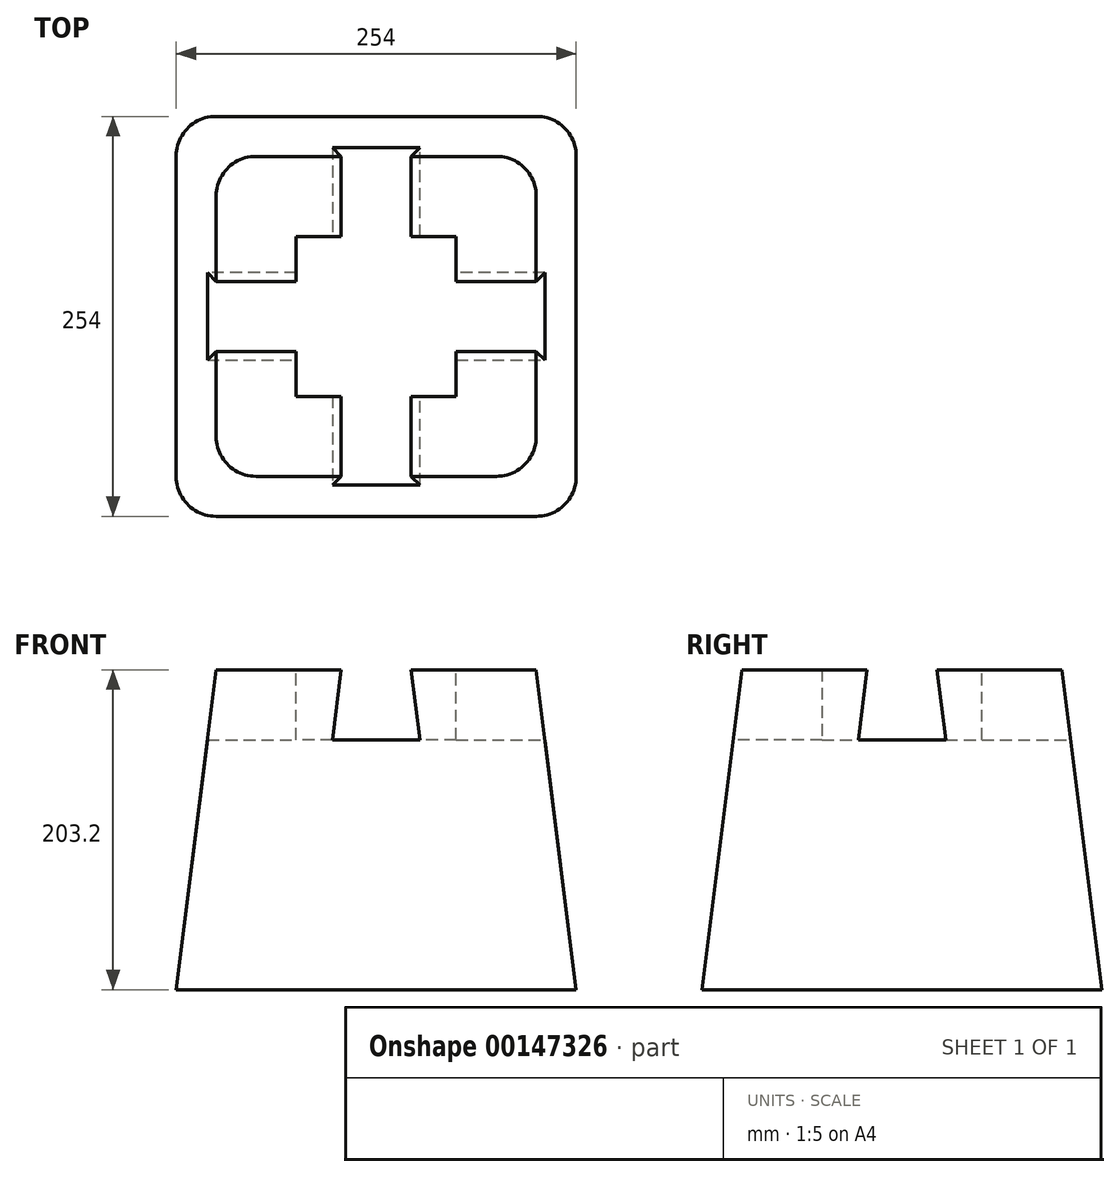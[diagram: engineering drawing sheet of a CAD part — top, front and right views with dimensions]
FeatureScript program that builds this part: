
annotation { "Feature Type Name" : "Feature", "Feature Type Description" : "" }
export const myFeature = defineFeature(function(context is Context, id is Id, definition is map)
    precondition{}
    {
        {
            var Q0;
            Q0=qCreatedBy(makeId("Top.planeOp"),FACE);
            var sketch = newSketch(context, id + "F0", { "sketchPlane" : qUnion([Q0])});
            skLineSegment(sketch, "E0.bottom", {"start": v(-127.47, 138) * mm, "end": v(126.53, 138) * mm});
            skLineSegment(sketch, "E0.top", {"start": v(-127.47, -116) * mm, "end": v(126.53, -116) * mm});
            skLineSegment(sketch, "E0.left", {"start": v(-127.47, 138) * mm, "end": v(-127.47, -116) * mm});
            skLineSegment(sketch, "E0.right", {"start": v(126.53, 138) * mm, "end": v(126.53, -116) * mm});
            skSolve(sketch);
        }
        {
            var Q0;
            Q0=qSketchRegion(id+"F0",true);
            extrude(context, id + "F1", {"entities" : qUnion([Q0]), "depth" : 203.2 * mm, "hasDraft" : true, "draftAngle" : 7.12 * degree, "draftPullDirection" : true});
        }
        {
            var Q0;
            Q0=makeQuery(id+"F1.opExtrude","SWEPT_EDGE",EDGE,{"disambiguationData":[OSD([sQuery(id+"F0.wireOp",EDGE,"E0.top"),sQuery(id+"F0.wireOp",EDGE,"E0.left")])]});
            var Q1;
            Q1=makeQuery(id+"F1.opExtrude","SWEPT_EDGE",EDGE,{"disambiguationData":[OSD([sQuery(id+"F0.wireOp",EDGE,"E0.top"),sQuery(id+"F0.wireOp",EDGE,"E0.right")])]});
            var Q2;
            Q2=makeQuery(id+"F1.opExtrude","SWEPT_EDGE",EDGE,{"disambiguationData":[OSD([sQuery(id+"F0.wireOp",EDGE,"E0.bottom"),sQuery(id+"F0.wireOp",EDGE,"E0.right")])]});
            var Q3;
            Q3=makeQuery(id+"F1.opExtrude","SWEPT_EDGE",EDGE,{"disambiguationData":[OSD([sQuery(id+"F0.wireOp",EDGE,"E0.bottom"),sQuery(id+"F0.wireOp",EDGE,"E0.left")])]});
            fillet(context, id + "F2", {"entities" : qUnion([Q0, Q1, Q2, Q3]), "radius" : 25.4 * mm, "tangentPropagation" : true, "allowEdgeOverflow" : false});
        }
        {
            var Q0;
            Q0=makeQuery(id+"F1.opExtrude","CAP_FACE",FACE,{"disambiguationData":[OSD([sQuery(id+"F0.wireOp",EDGE,"E0.bottom"),sQuery(id+"F0.wireOp",EDGE,"E0.top"),sQuery(id+"F0.wireOp",EDGE,"E0.left"),sQuery(id+"F0.wireOp",EDGE,"E0.right")])],"isStart":false});
            var sketch = newSketch(context, id + "F3", { "sketchPlane" : qUnion([Q0])});
            skLineSegment(sketch, "E1.0", {"start": v(-102.07, 33.23) * mm, "end": v(-102.07, -11.22) * mm});
            skLineSegment(sketch, "E2.0", {"start": v(-22.7, 112.6) * mm, "end": v(21.76, 112.6) * mm});
            skLineSegment(sketch, "E3.0", {"start": v(-22.7, -90.6) * mm, "end": v(21.76, -90.6) * mm});
            skLineSegment(sketch, "E4.0", {"start": v(101.13, 33.23) * mm, "end": v(101.13, -11.22) * mm});
            skLineSegment(sketch, "E5.bottom", {"start": v(-102.07, -11.22) * mm, "end": v(-22.7, -11.22) * mm});
            skLineSegment(sketch, "E5.top", {"start": v(-102.07, 33.23) * mm, "end": v(-22.7, 33.23) * mm});
            skLineSegment(sketch, "E5.left", {"start": v(-102.07, -11.22) * mm, "end": v(-102.07, 33.23) * mm});
            skLineSegment(sketch, "E5.right", {"start": v(101.13, -11.22) * mm, "end": v(101.13, 33.23) * mm});
            skLineSegment(sketch, "E6.left", {"start": v(-22.7, -90.6) * mm, "end": v(-22.7, -11.22) * mm});
            skLineSegment(sketch, "E6.right", {"start": v(21.76, -90.6) * mm, "end": v(21.76, -11.22) * mm});
            skLineSegment(sketch, "E7.trimOffspring", {"start": v(-22.7, 33.23) * mm, "end": v(-22.7, 112.6) * mm});
            skLineSegment(sketch, "E8.trimOffspring", {"start": v(21.76, 33.23) * mm, "end": v(101.13, 33.23) * mm});
            skLineSegment(sketch, "E9.trimOffspring", {"start": v(21.76, 33.23) * mm, "end": v(21.76, 112.6) * mm});
            skLineSegment(sketch, "E10.trimOffspring", {"start": v(21.76, -11.22) * mm, "end": v(101.13, -11.22) * mm});
            skPoint(sketch, "E11.orphan", {"position": v(101.13, -65.4) * mm});
            skPoint(sketch, "E12.orphan", {"position": v(101.13, 87.4) * mm});
            skPoint(sketch, "E13.orphan", {"position": v(75.93, 112.6) * mm});
            skPoint(sketch, "E14.orphan", {"position": v(-76.86, 112.6) * mm});
            skPoint(sketch, "E15.orphan", {"position": v(-102.07, 87.4) * mm});
            skPoint(sketch, "E16.orphan", {"position": v(-102.07, -65.4) * mm});
            skPoint(sketch, "E17.orphan", {"position": v(-76.86, -90.6) * mm});
            skPoint(sketch, "E18.orphan", {"position": v(75.93, -90.6) * mm});
            skSolve(sketch);
        }
        {
            var Q0;
            Q0=qSketchRegion(id+"F3",true);
            extrude(context, id + "F4", {"entities" : qUnion([Q0]), "operationType" : NewBodyOperationType.REMOVE, "oppositeDirection" : true, "depth" : 44.45 * mm, "hasDraft" : true, "draftAngle" : 7.12 * degree});
        }
        {
            var Q0;
            {var subQ0=sQuery(id+"F0.wireOp",EDGE,"E0.left");var subQ1=sQuery(id+"F0.wireOp",EDGE,"E0.top");Q0=makeQuery(id+"F4.boolean.opBoolean","SPLIT",FACE,{"disambiguationData":[TD([makeQuery(id+"F4.opExtrude","SWEPT_FACE",FACE,{"disambiguationData":[OSD([sQuery(id+"F3.wireOp",EDGE,"E5.bottom")])]})])],"derivedFrom":makeQuery(id+"F1.opExtrude","CAP_FACE",FACE,{"disambiguationData":[OSD([sQuery(id+"F0.wireOp",EDGE,"E0.bottom"),subQ1,subQ0,sQuery(id+"F0.wireOp",EDGE,"E0.right")])],"isStart":false})});}
            var sketch = newSketch(context, id + "F5", { "sketchPlane" : qUnion([Q0])});
            skLineSegment(sketch, "E19.bottom", {"start": v(50.33, -39.8) * mm, "end": v(-51.27, -39.8) * mm});
            skLineSegment(sketch, "E19.top", {"start": v(50.33, 61.8) * mm, "end": v(-51.27, 61.8) * mm});
            skLineSegment(sketch, "E19.left", {"start": v(50.33, -39.8) * mm, "end": v(50.33, 61.8) * mm});
            skLineSegment(sketch, "E19.right", {"start": v(-51.27, -39.8) * mm, "end": v(-51.27, 61.8) * mm});
            skPoint(sketch, "E20.0.end.orphan", {"position": v(75.93, -90.6) * mm});
            skPoint(sketch, "E20.0.start.orphan", {"position": v(21.76, -90.6) * mm});
            skPoint(sketch, "E21.0.end.orphan", {"position": v(101.13, -65.4) * mm});
            skPoint(sketch, "E21.0.start.orphan", {"position": v(101.13, -11.22) * mm});
            skSolve(sketch);
        }
        {
            var Q0;
            Q0=qSketchRegion(id+"F5",true);
            extrude(context, id + "F6", {"entities" : qUnion([Q0]), "operationType" : NewBodyOperationType.REMOVE, "oppositeDirection" : true, "depth" : 44.45 * mm});
        }
    });
